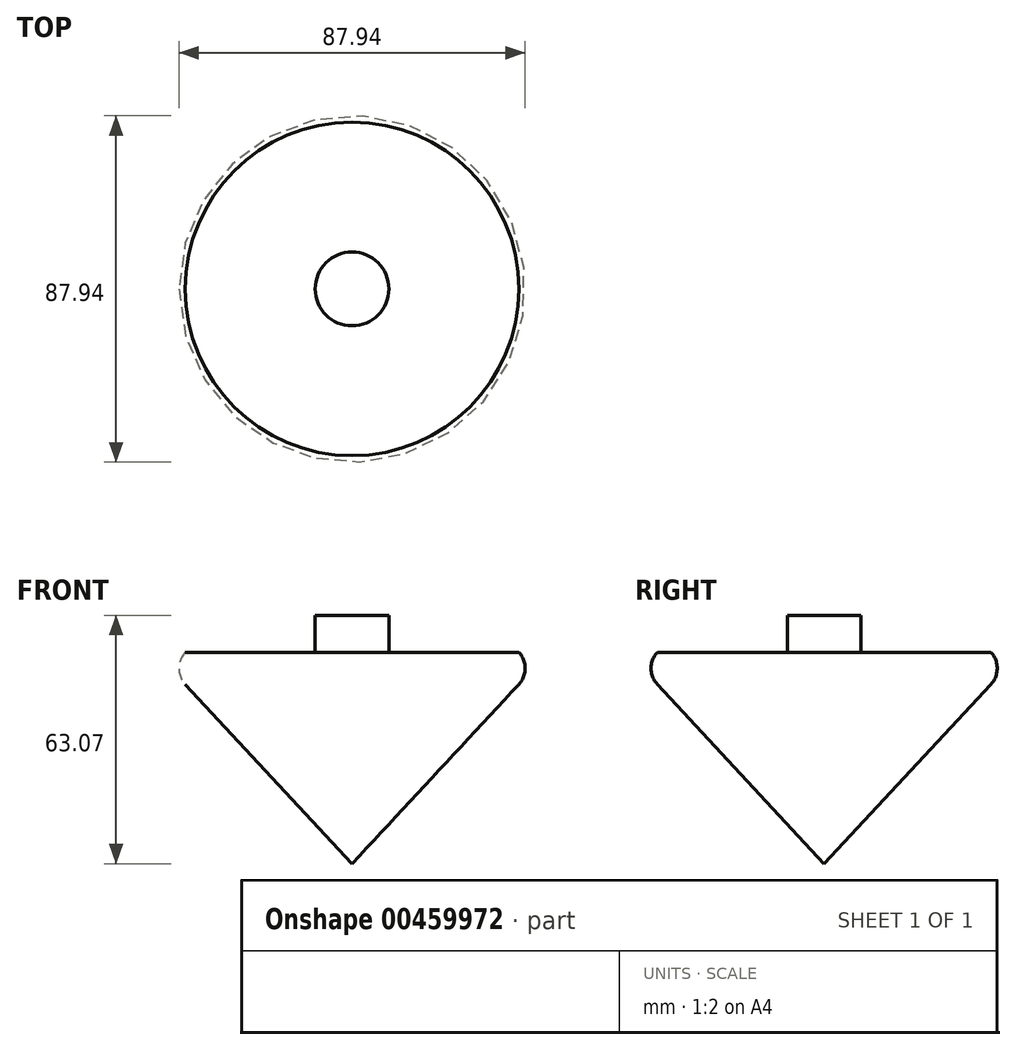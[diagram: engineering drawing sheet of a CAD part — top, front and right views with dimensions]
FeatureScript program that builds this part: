
annotation { "Feature Type Name" : "Feature", "Feature Type Description" : "" }
export const myFeature = defineFeature(function(context is Context, id is Id, definition is map)
    precondition{}
    {
        {
            var Q0;
            Q0=qCreatedBy(makeId("Front.planeOp"),FACE);
            var sketch = newSketch(context, id + "F0", { "sketchPlane" : qUnion([Q0])});
            skLineSegment(sketch, "E0", {"start": v(0, 0) * mm, "end": v(0, 63.07) * mm});
            skLineSegment(sketch, "E1", {"start": v(0, 63.07) * mm, "end": v(9.37, 63.07) * mm});
            skLineSegment(sketch, "E2", {"start": v(9.37, 63.07) * mm, "end": v(9.37, 53.71) * mm});
            skLineSegment(sketch, "E3", {"start": v(9.37, 53.71) * mm, "end": v(42.37, 53.71) * mm});
            skLineSegment(sketch, "E4", {"start": v(0, 0) * mm, "end": v(42.37, 45.57) * mm});
            skArc(sketch, "E5", {"start": v(42.37, 45.57) * mm, "mid": v(43.97, 49.64) * mm, "end": v(42.37, 53.71) * mm});
            skSolve(sketch);
        }
        {
            var Q0;
            Q0=makeQuery(id+"F0.imprint","IMPRINT",FACE,{"disambiguationData":[TD([[makeQuery(id+"F0.imprint","IMPRINT",EDGE,{"derivedFrom":sQuery(id+"F0.wireOp",EDGE,"E0")}),-1.0]])]});
            var Q1;
            Q1 = qSketchRegion(id + "FVBFc6HXWvKVK5p_1", true);
            var Q2;
            Q2=sQuery(id+"F0.wireOp",EDGE,"E0");
            revolve(context, id + "F1", {"entities" : qUnion([Q0, Q1]), "axis" : qUnion([Q2]), "revolveType" : RevolveType.FULL});
        }
    });
